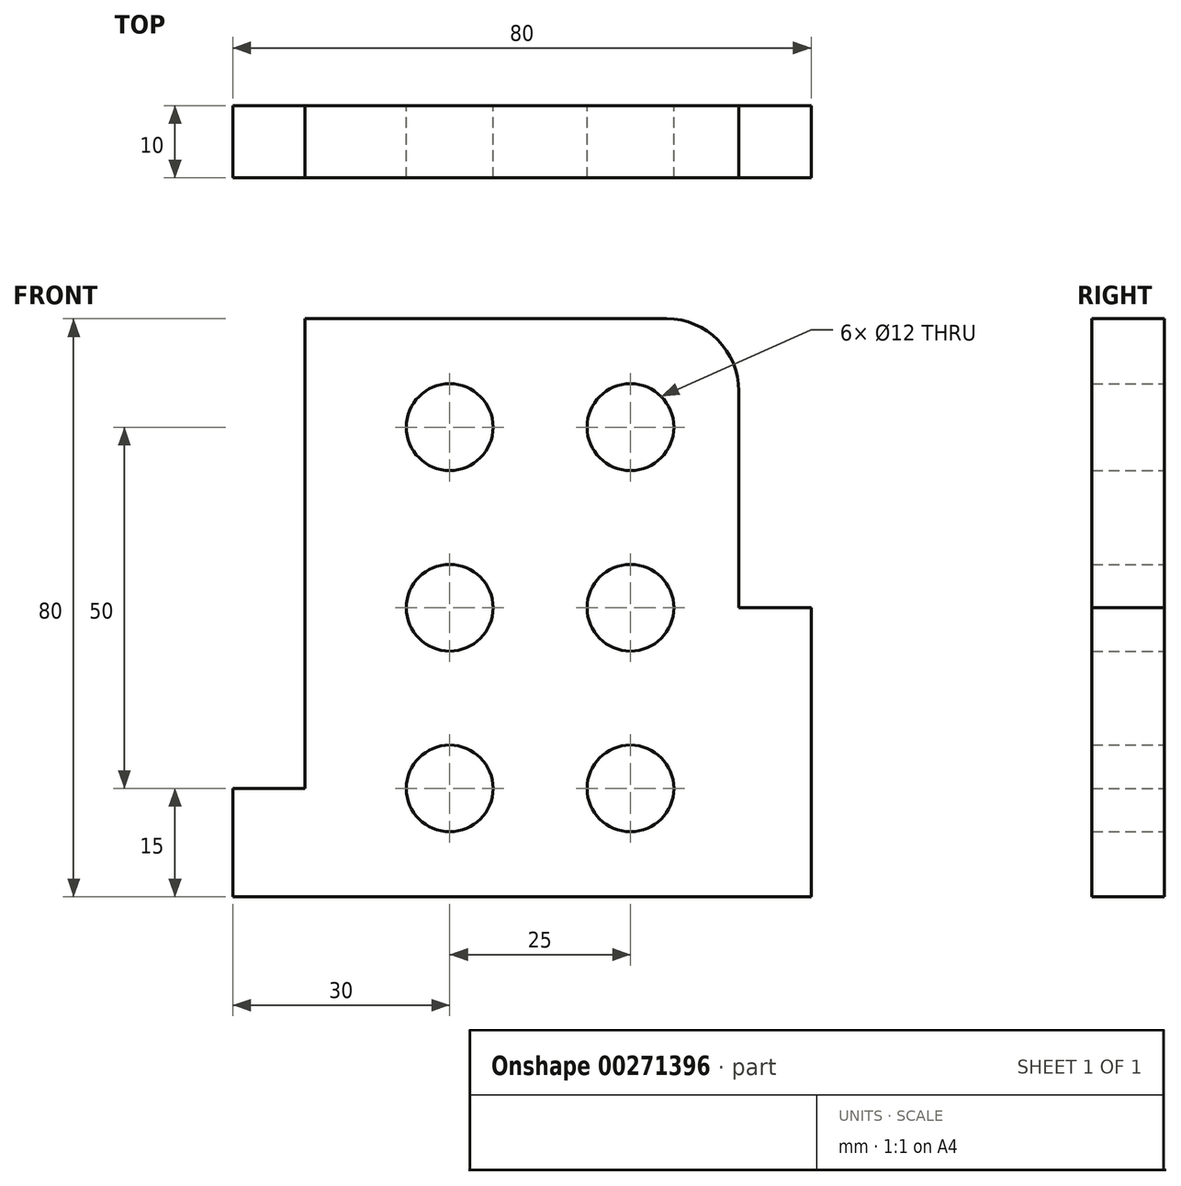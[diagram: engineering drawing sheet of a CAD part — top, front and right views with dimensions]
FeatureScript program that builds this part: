
annotation { "Feature Type Name" : "Feature", "Feature Type Description" : "" }
export const myFeature = defineFeature(function(context is Context, id is Id, definition is map)
    precondition{}
    {
        {
            var Q0;
            Q0=qCreatedBy(makeId("Front.planeOp"),FACE);
            var sketch = newSketch(context, id + "F0", { "sketchPlane" : qUnion([Q0])});
            skLineSegment(sketch, "E0", {"start": v(0, 0) * mm, "end": v(80, 0) * mm});
            skLineSegment(sketch, "E1", {"start": v(80, 0) * mm, "end": v(80, 40) * mm});
            skLineSegment(sketch, "E2", {"start": v(80, 40) * mm, "end": v(70, 40) * mm});
            skLineSegment(sketch, "E3", {"start": v(0, 0) * mm, "end": v(0, 15) * mm});
            skLineSegment(sketch, "E4", {"start": v(0, 15) * mm, "end": v(10, 15) * mm});
            skLineSegment(sketch, "E5", {"start": v(10, 15) * mm, "end": v(10, 80) * mm});
            skLineSegment(sketch, "E6", {"start": v(10, 80) * mm, "end": v(60, 80) * mm});
            skLineSegment(sketch, "E7", {"start": v(70, 40) * mm, "end": v(70, 70) * mm});
            skCircle(sketch, "E8", {"center": v(30, 15) * mm, "radius": 6 * mm});
            skCircle(sketch, "E9", {"center": v(30, 40) * mm, "radius": 6 * mm});
            skCircle(sketch, "E10", {"center": v(55, 15) * mm, "radius": 6 * mm});
            skCircle(sketch, "E11", {"center": v(55, 40) * mm, "radius": 6 * mm});
            skCircle(sketch, "E12", {"center": v(30, 65) * mm, "radius": 6 * mm});
            skCircle(sketch, "E13", {"center": v(55, 65) * mm, "radius": 6 * mm});
            skArc(sketch, "E14", {"start": v(70, 70) * mm, "mid": v(67.07, 77.07) * mm, "end": v(60, 80) * mm});
            skSolve(sketch);
        }
        {
            var Q0;
            Q0 = qSketchRegion(id + "F0", true);
            extrude(context, id + "F1", {"entities" : qUnion([Q0]), "depth" : 10 * mm});
        }
    });
